# Revit family: 30_HBE0753DK
name_source: partatom
category: Equipos especializados
units: mm (PartAtom-declared; Revit-internal decimal feet)

## family parameters
Compartido = Sí
Corte con vacíos al cargar = Sí
Cota de conector redondo = Diámetro de uso
Punto de cálculo de habitación = No
Se basa en plano de trabajo = Sí
Siempre vertical = Sí
Tipo de pieza = Normal

## types (1)
- HBE0753DK
    Ancho = 58 cm
    Aprobaciones = CE/GS/CB/SAA
    Bloqueo de seguridad para niños = Si
    Control del nivel de temperatura = 9 Niveles
    Controles = Touch
    Creado por = Unibim
    Cubierta = Vidrio Cerámico Negro
    Descripción = Empotrable 4 Platos Control Digital Touch
    Elevación por defecto = 122 cm
    Encimera = Iron, Gray
    Especificación Técnica = Empotrable 4 Platos Control Digital Touch
    Fabricante = Vatti
    Fondo = 51 cm
    Indicador de temperatura residual = Si
    Modelo = HBE0753DK
    Modo de Control = Control digital touch
    Paneles = Vitro ceramico
    Potencia Maxima total = 6,0 kW
    Potencia Zona 1 = 1.8 kW / 200mm
    Potencia Zona 2 = 1.2 kW / 165mm
    Potencia Zona 3 = 1.8 kW / 200mm
    Potencia Zona 4 = 1.2 kW / 165mm
    Potencia Zona 5 = -
    Protección de sobrecalentamiento = Doble
    Quemador = _Quemador
    Tamaño del corte en superficie = 580 x 510 x 50mm
    Tamaño del producto = 560 x 490 R20
    Termostato Individual por plato = Si
    Tipo = Empotrable 4 Platos Control Digital Touch
    URL = www.vatti.cl
    Zonas = 4

## geometry (parser evidence)
native form markers: Sweep x4
no freeform markers — native parametric forms only
